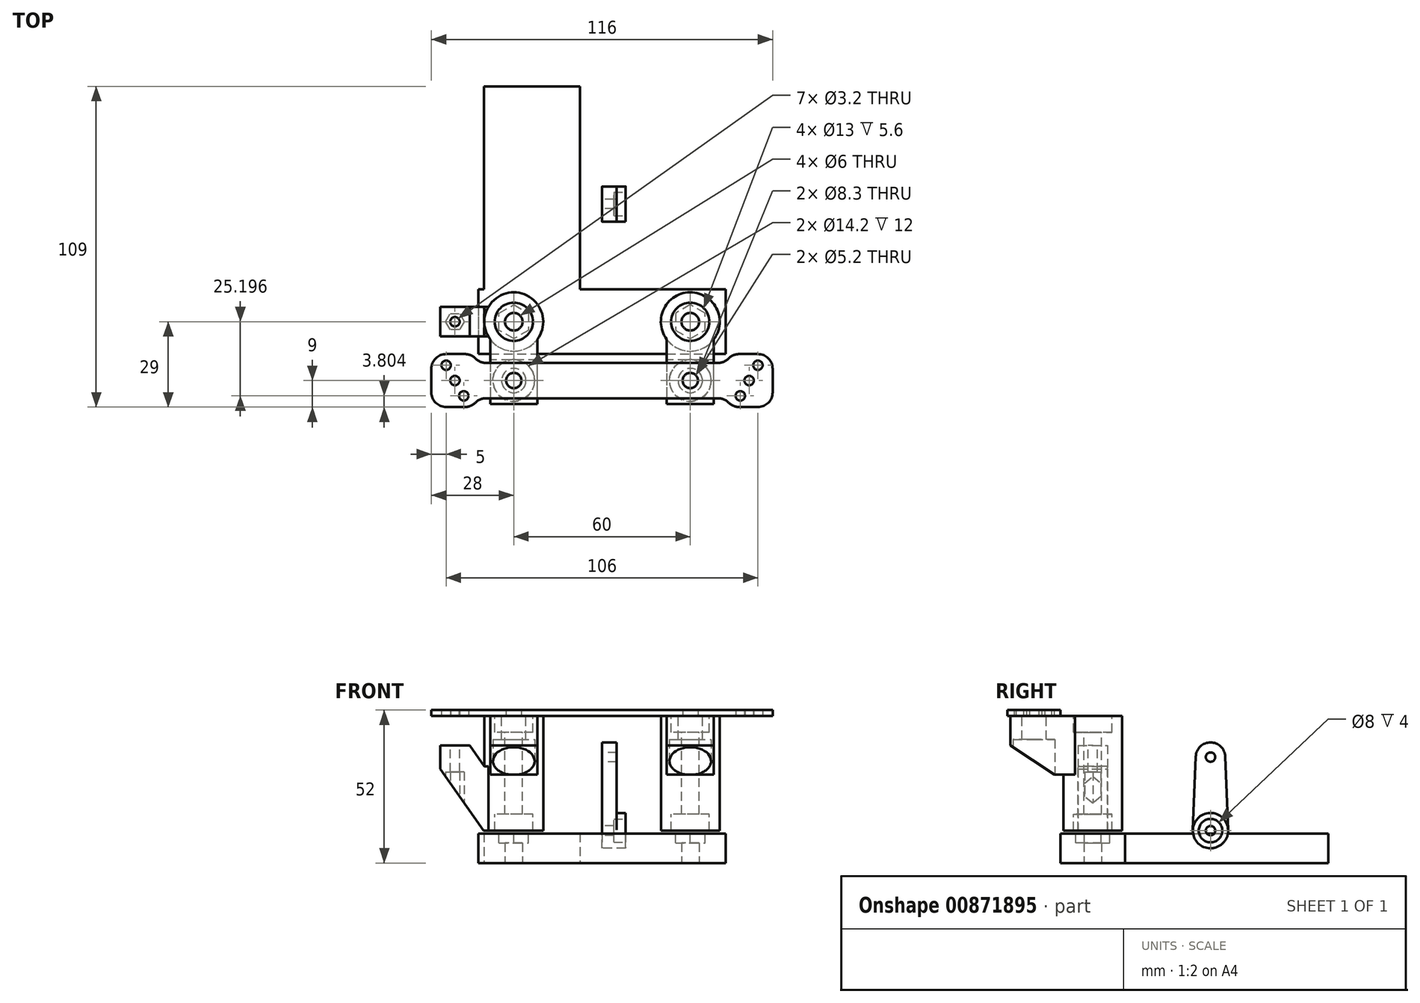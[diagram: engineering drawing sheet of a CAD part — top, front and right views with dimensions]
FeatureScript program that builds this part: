
annotation { "Feature Type Name" : "Feature", "Feature Type Description" : "" }
export const myFeature = defineFeature(function(context is Context, id is Id, definition is map)
    precondition{}
    {
        {
            var Q0;
            Q0=qCreatedBy(makeId("Top.planeOp"),FACE);
            var sketch = newSketch(context, id + "F0", { "sketchPlane" : qUnion([Q0])});
            skCircle(sketch, "E0", {"center": v(-30, 0) * mm, "radius": 3 * mm});
            skCircle(sketch, "E1", {"center": v(30, 0) * mm, "radius": 3 * mm});
            skLineSegment(sketch, "E2.bottom", {"start": v(-42, 11) * mm, "end": v(42, 11) * mm});
            skLineSegment(sketch, "E2.top", {"start": v(-42, -11) * mm, "end": v(42, -11) * mm});
            skLineSegment(sketch, "E2.left", {"start": v(-42, 11) * mm, "end": v(-42, -11) * mm});
            skLineSegment(sketch, "E2.right", {"start": v(42, 11) * mm, "end": v(42, -11) * mm});
            skPoint(sketch, "E2.middle", {"position": v(0, 0) * mm});
            skLineSegment(sketch, "E3", {"start": v(-30, 0) * mm, "end": v(30, 0) * mm, "construction": true});
            skSolve(sketch);
        }
        {
            var Q0;
            Q0=qSketchRegion(id+"F0",true);
            extrude(context, id + "F1", {"entities" : qUnion([Q0]), "depth" : 10 * mm, "offsetDistance" : 25 * mm});
        }
        {
            var Q0;
            Q0=makeQuery(id+"F1.opExtrude","CAP_FACE",FACE,{"disambiguationData":[OSD([sQuery(id+"F0.wireOp",EDGE,"E0"),sQuery(id+"F0.wireOp",EDGE,"E1"),sQuery(id+"F0.wireOp",EDGE,"E2.bottom"),sQuery(id+"F0.wireOp",EDGE,"E2.top"),sQuery(id+"F0.wireOp",EDGE,"E2.left"),sQuery(id+"F0.wireOp",EDGE,"E2.right")])],"isStart":false});
            var sketch = newSketch(context, id + "F2", { "sketchPlane" : qUnion([Q0])});
            skCircle(sketch, "E4.cCircle", {"center": v(-30, 0) * mm, "radius": 5 * mm, "construction": true});
            skLineSegment(sketch, "E4.0", {"start": v(-25, 2.89) * mm, "end": v(-25, -2.89) * mm});
            skLineSegment(sketch, "E4.1", {"start": v(-25, -2.89) * mm, "end": v(-30, -5.77) * mm});
            skLineSegment(sketch, "E4.2", {"start": v(-30, -5.77) * mm, "end": v(-35, -2.89) * mm});
            skLineSegment(sketch, "E4.3", {"start": v(-35, -2.89) * mm, "end": v(-35, 2.89) * mm});
            skLineSegment(sketch, "E4.4", {"start": v(-35, 2.89) * mm, "end": v(-30, 5.77) * mm});
            skLineSegment(sketch, "E4.5", {"start": v(-30, 5.77) * mm, "end": v(-25, 2.89) * mm});
            skPoint(sketch, "E4.0.midPoint", {"position": v(-25, 0) * mm});
            skLineSegment(sketch, "E5", {"start": v(0, 0) * mm, "end": v(0, 13.19) * mm, "construction": true});
            skLineSegment(sketch, "E6.MirrorCS", {"start": v(25, -2.89) * mm, "end": v(30, -5.77) * mm});
            skLineSegment(sketch, "E7.MirrorCS", {"start": v(35, 2.89) * mm, "end": v(30, 5.77) * mm});
            skPoint(sketch, "E8.MirrorP", {"position": v(25, 0) * mm});
            skCircle(sketch, "E9.MirrorC", {"center": v(30, 0) * mm, "radius": 5 * mm, "construction": true});
            skLineSegment(sketch, "E10.MirrorCS", {"start": v(25, 2.89) * mm, "end": v(25, -2.89) * mm});
            skLineSegment(sketch, "E11.MirrorCS", {"start": v(30, -5.77) * mm, "end": v(35, -2.89) * mm});
            skLineSegment(sketch, "E12.MirrorCS", {"start": v(35, -2.89) * mm, "end": v(35, 2.89) * mm});
            skLineSegment(sketch, "E13.MirrorCS", {"start": v(30, 5.77) * mm, "end": v(25, 2.89) * mm});
            skSolve(sketch);
        }
        {
            var Q0;
            Q0=qSketchRegion(id+"F2",true);
            extrude(context, id + "F3", {"entities" : qUnion([Q0]), "operationType" : NewBodyOperationType.REMOVE, "oppositeDirection" : true, "depth" : 3.2 * mm, "offsetDistance" : 25 * mm});
        }
        {
            var Q0;
            Q0=qCreatedBy(makeId("Front.planeOp"),FACE);
            var sketch = newSketch(context, id + "F4", { "sketchPlane" : qUnion([Q0])});
            skLineSegment(sketch, "E14", {"start": v(-30, 31.7) * mm, "end": v(-30, -19.85) * mm, "construction": true});
            skLineSegment(sketch, "E15", {"start": v(0, 0) * mm, "end": v(0, 44.27) * mm, "construction": true});
            skLineSegment(sketch, "E16.bottom", {"start": v(-40, 11) * mm, "end": v(-36.5, 11) * mm});
            skLineSegment(sketch, "E16.top", {"start": v(-40, 50) * mm, "end": v(-36.5, 50) * mm});
            skLineSegment(sketch, "E16.left", {"start": v(-40, 11) * mm, "end": v(-40, 50) * mm});
            skLineSegment(sketch, "E17.right", {"start": v(-36.5, 11) * mm, "end": v(-36.5, 16.6) * mm});
            skLineSegment(sketch, "E18", {"start": v(-33, 44.4) * mm, "end": v(-33, 16.6) * mm});
            skLineSegment(sketch, "E19.trimOffspring", {"start": v(-33, 16.6) * mm, "end": v(-36.5, 16.6) * mm});
            skLineSegment(sketch, "E20", {"start": v(-40, 30.5) * mm, "end": v(-16.74, 30.5) * mm, "construction": true});
            skLineSegment(sketch, "E21.MirrorCS", {"start": v(-33, 44.4) * mm, "end": v(-36.5, 44.4) * mm});
            skLineSegment(sketch, "E22.MirrorCS", {"start": v(-36.5, 50) * mm, "end": v(-36.5, 44.4) * mm});
            skSolve(sketch);
        }
        {
            var Q0;
            Q0=makeQuery(id+"F4.imprint","IMPRINT",FACE,{"disambiguationData":[TD([[makeQuery(id+"F4.imprint","IMPRINT",EDGE,{"derivedFrom":sQuery(id+"F4.wireOp",EDGE,"E16.bottom")}),1.0]])]});
            var Q1;
            Q1=sQuery(id+"F4.wireOp",EDGE,"E14");
            revolve(context, id + "F5", {"surfaceOperationType" : NewSurfaceOperationType.NEW, "entities" : qUnion([Q0]), "axis" : qUnion([Q1]), "revolveType" : RevolveType.FULL});
        }
        {
            var Q0;
            Q0=makeQuery(id+"F5.opRevolve","SWEPT_FACE",FACE,{"disambiguationData":[OSD([sQuery(id+"F4.wireOp",EDGE,"E16.top")])]});
            var sketch = newSketch(context, id + "F6", { "sketchPlane" : qUnion([Q0])});
            skArc(sketch, "E23.0", {"start": v(-38, -6) * mm, "mid": v(-30, -10) * mm, "end": v(-22, -6) * mm});
            skLineSegment(sketch, "E24", {"start": v(-38, -6) * mm, "end": v(-38, -28) * mm});
            skLineSegment(sketch, "E25", {"start": v(-38, -28) * mm, "end": v(-22, -28) * mm});
            skLineSegment(sketch, "E26", {"start": v(-22, -28) * mm, "end": v(-22, -6) * mm});
            skLineSegment(sketch, "E27", {"start": v(-30, 0) * mm, "end": v(-30, -20) * mm, "construction": true});
            skCircle(sketch, "E28", {"center": v(-30, -20) * mm, "radius": 4.15 * mm});
            skSolve(sketch);
        }
        {
            var Q0;
            Q0=qSketchRegion(id+"F6",true);
            extrude(context, id + "F7", {"entities" : qUnion([Q0]), "operationType" : NewBodyOperationType.ADD, "oppositeDirection" : true, "depth" : 20 * mm, "offsetDistance" : 25 * mm});
        }
        {
            var Q0;
            Q0=makeQuery(id+"F7.opExtrude","CAP_EDGE",EDGE,{"disambiguationData":[OSD([sQuery(id+"F6.wireOp",EDGE,"E25")])],"isStart":false});
            chamfer(context, id + "F8", {"entities" : qUnion([Q0]), "chamferType" : ChamferType.TWO_OFFSETS, "width1" : 10 * mm, "oppositeDirection" : false, "width2" : 15 * mm, "tangentPropagation" : true});
        }
        {
            var Q0;
            Q0=makeQuery(id+"F7.opExtrude","CAP_FACE",FACE,{"disambiguationData":[OSD([sQuery(id+"F6.wireOp",EDGE,"E23.0"),sQuery(id+"F6.wireOp",EDGE,"E24"),sQuery(id+"F6.wireOp",EDGE,"E25"),sQuery(id+"F6.wireOp",EDGE,"E26"),sQuery(id+"F6.wireOp",EDGE,"E28")])],"isStart":false});
            var sketch = newSketch(context, id + "F9", { "sketchPlane" : qUnion([Q0])});
            skCircle(sketch, "E29.0", {"center": v(-30, 20) * mm, "radius": 4.15 * mm, "construction": true});
            skCircle(sketch, "E30.cCircle", {"center": v(-30, 20) * mm, "radius": 7.1 * mm});
            skLineSegment(sketch, "E30.0", {"start": v(-34.1, 27.1) * mm, "end": v(-25.9, 27.1) * mm, "construction": true});
            skLineSegment(sketch, "E30.1", {"start": v(-25.9, 27.1) * mm, "end": v(-21.8, 20) * mm, "construction": true});
            skLineSegment(sketch, "E30.2", {"start": v(-21.8, 20) * mm, "end": v(-25.9, 12.9) * mm, "construction": true});
            skLineSegment(sketch, "E30.3", {"start": v(-25.9, 12.9) * mm, "end": v(-34.1, 12.9) * mm, "construction": true});
            skLineSegment(sketch, "E30.4", {"start": v(-34.1, 12.9) * mm, "end": v(-38.2, 20) * mm, "construction": true});
            skLineSegment(sketch, "E30.5", {"start": v(-38.2, 20) * mm, "end": v(-34.1, 27.1) * mm, "construction": true});
            skPoint(sketch, "E30.0.midPoint", {"position": v(-30, 27.1) * mm});
            skSolve(sketch);
        }
        {
            var Q0;
            Q0=qSketchRegion(id+"F9",true);
            extrude(context, id + "F10", {"entities" : qUnion([Q0]), "operationType" : NewBodyOperationType.REMOVE, "oppositeDirection" : true, "depth" : 12 * mm, "offsetDistance" : 25 * mm});
        }
        {
            var Q0;
            Q0=makeQuery(id+"F5.opRevolve","SWEPT_BODY",BODY,{"disambiguationData":[OSD([sQuery(id+"F4.wireOp",EDGE,"E16.bottom"),sQuery(id+"F4.wireOp",EDGE,"E16.top"),sQuery(id+"F4.wireOp",EDGE,"E16.left"),sQuery(id+"F4.wireOp",EDGE,"E17.right"),sQuery(id+"F4.wireOp",EDGE,"E18"),sQuery(id+"F4.wireOp",EDGE,"E19.trimOffspring"),sQuery(id+"F4.wireOp",EDGE,"E21.MirrorCS"),sQuery(id+"F4.wireOp",EDGE,"E22.MirrorCS")])]});
            transform(context, id + "F11", {"entities" : qUnion([Q0]), "transformType" : TransformType.TRANSLATION_3D, "dx" : 60 * mm, "dy" : 0 * mm, "dz" : 0 * mm, "makeCopy" : true});
        }
        {
            var Q0;
            Q0=makeQuery(id+"F11.opPattern","COPY",FACE,{"derivedFrom":makeQuery(id+"F7.boolean.opBoolean","MERGE",FACE,{"derivedFrom":[makeQuery(id+"F5.opRevolve","SWEPT_FACE",FACE,{"disambiguationData":[OSD([sQuery(id+"F4.wireOp",EDGE,"E16.top")])]}),makeQuery(id+"F7.opExtrude","CAP_FACE",FACE,{"disambiguationData":[OSD([sQuery(id+"F6.wireOp",EDGE,"E23.0"),sQuery(id+"F6.wireOp",EDGE,"E24"),sQuery(id+"F6.wireOp",EDGE,"E25"),sQuery(id+"F6.wireOp",EDGE,"E26"),sQuery(id+"F6.wireOp",EDGE,"E28")])],"isStart":true})]}),"instanceName":"1"});
            var sketch = newSketch(context, id + "F12", { "sketchPlane" : qUnion([Q0])});
            skLineSegment(sketch, "E31", {"start": v(-50, -20) * mm, "end": v(50, -20) * mm, "construction": true});
            skLineSegment(sketch, "E32", {"start": v(0, 0) * mm, "end": v(0, -26) * mm, "construction": true});
            skLineSegment(sketch, "E33.bottom", {"start": v(42, -26) * mm, "end": v(0, -26) * mm});
            skPoint(sketch, "E33.middle", {"position": v(0, -20) * mm});
            skLineSegment(sketch, "E34", {"start": v(47, -25.2) * mm, "end": v(53, -14.8) * mm, "construction": true});
            skPoint(sketch, "E34.endSnap0", {"position": v(38, -17) * mm});
            skLineSegment(sketch, "E35.bottom", {"start": v(58, -11) * mm, "end": v(42, -11) * mm});
            skLineSegment(sketch, "E35.top", {"start": v(58, -29) * mm, "end": v(42, -29) * mm});
            skLineSegment(sketch, "E35.right", {"start": v(42, -11) * mm, "end": v(42, -14) * mm});
            skPoint(sketch, "E35.middle", {"position": v(50, -20) * mm});
            skCircle(sketch, "E36", {"center": v(53, -14.8) * mm, "radius": 1.6 * mm});
            skCircle(sketch, "E37", {"center": v(50, -20) * mm, "radius": 1.6 * mm});
            skCircle(sketch, "E38", {"center": v(47, -25.2) * mm, "radius": 1.6 * mm});
            skLineSegment(sketch, "E39.trimOffspring", {"start": v(42, -14) * mm, "end": v(0, -14) * mm});
            skLineSegment(sketch, "E40.trimOffspring", {"start": v(42, -26) * mm, "end": v(42, -29) * mm});
            skLineSegment(sketch, "E41", {"start": v(58, -11) * mm, "end": v(58, -29) * mm});
            skCircle(sketch, "E42.MirrorC", {"center": v(-50, -20) * mm, "radius": 1.6 * mm});
            skLineSegment(sketch, "E43.MirrorCS", {"start": v(-58, -11) * mm, "end": v(-58, -29) * mm});
            skLineSegment(sketch, "E44.MirrorCS", {"start": v(-58, -11) * mm, "end": v(-42, -11) * mm});
            skLineSegment(sketch, "E45.MirrorCS", {"start": v(-58, -29) * mm, "end": v(-42, -29) * mm});
            skLineSegment(sketch, "E46.MirrorCS", {"start": v(-42, -14) * mm, "end": v(0, -14) * mm});
            skPoint(sketch, "E47.MirrorP", {"position": v(-38, -17) * mm});
            skCircle(sketch, "E48.MirrorC", {"center": v(-53, -14.8) * mm, "radius": 1.6 * mm});
            skLineSegment(sketch, "E49.MirrorCS", {"start": v(-42, -26) * mm, "end": v(-42, -29) * mm});
            skLineSegment(sketch, "E50.MirrorCS", {"start": v(-47, -25.2) * mm, "end": v(-53, -14.8) * mm, "construction": true});
            skLineSegment(sketch, "E51.MirrorCS", {"start": v(-42, -11) * mm, "end": v(-42, -14) * mm});
            skLineSegment(sketch, "E52.MirrorCS", {"start": v(50, -20) * mm, "end": v(-50, -20) * mm, "construction": true});
            skLineSegment(sketch, "E53.MirrorCS", {"start": v(-42, -26) * mm, "end": v(0, -26) * mm});
            skCircle(sketch, "E54.MirrorC", {"center": v(-47, -25.2) * mm, "radius": 1.6 * mm});
            skCircle(sketch, "E55.0", {"center": v(30, -20) * mm, "radius": 4.15 * mm, "construction": true});
            skCircle(sketch, "E56.0", {"center": v(-30, -20) * mm, "radius": 4.15 * mm, "construction": true});
            skCircle(sketch, "E57", {"center": v(-30, -20) * mm, "radius": 2.6 * mm});
            skCircle(sketch, "E58", {"center": v(30, -20) * mm, "radius": 2.6 * mm});
            skSolve(sketch);
        }
        {
            var Q0;
            Q0=qSketchRegion(id+"F12",true);
            extrude(context, id + "F13", {"entities" : qUnion([Q0]), "depth" : 2 * mm, "offsetDistance" : 25 * mm});
        }
        {
            var Q0;
            Q0=makeQuery(id+"F13.opExtrude","SWEPT_EDGE",EDGE,{"disambiguationData":[OSD([sQuery(id+"F12.wireOp",EDGE,"E43.MirrorCS"),sQuery(id+"F12.wireOp",EDGE,"E45.MirrorCS")])]});
            var Q1;
            Q1=makeQuery(id+"F13.opExtrude","SWEPT_EDGE",EDGE,{"disambiguationData":[OSD([sQuery(id+"F12.wireOp",EDGE,"E45.MirrorCS"),sQuery(id+"F12.wireOp",EDGE,"E49.MirrorCS")])]});
            var Q2;
            Q2=makeQuery(id+"F13.opExtrude","SWEPT_EDGE",EDGE,{"disambiguationData":[OSD([sQuery(id+"F12.wireOp",EDGE,"E43.MirrorCS"),sQuery(id+"F12.wireOp",EDGE,"E44.MirrorCS")])]});
            var Q3;
            Q3=makeQuery(id+"F13.opExtrude","SWEPT_EDGE",EDGE,{"disambiguationData":[OSD([sQuery(id+"F12.wireOp",EDGE,"E44.MirrorCS"),sQuery(id+"F12.wireOp",EDGE,"E51.MirrorCS")])]});
            var Q4;
            Q4=makeQuery(id+"F13.opExtrude","SWEPT_EDGE",EDGE,{"disambiguationData":[OSD([sQuery(id+"F12.wireOp",EDGE,"E35.top"),sQuery(id+"F12.wireOp",EDGE,"E40.trimOffspring")])]});
            var Q5;
            Q5=makeQuery(id+"F13.opExtrude","SWEPT_EDGE",EDGE,{"disambiguationData":[OSD([sQuery(id+"F12.wireOp",EDGE,"E35.top"),sQuery(id+"F12.wireOp",EDGE,"E41")])]});
            var Q6;
            Q6=makeQuery(id+"F13.opExtrude","SWEPT_EDGE",EDGE,{"disambiguationData":[OSD([sQuery(id+"F12.wireOp",EDGE,"E35.bottom"),sQuery(id+"F12.wireOp",EDGE,"E35.right")])]});
            var Q7;
            Q7=makeQuery(id+"F13.opExtrude","SWEPT_EDGE",EDGE,{"disambiguationData":[OSD([sQuery(id+"F12.wireOp",EDGE,"E35.bottom"),sQuery(id+"F12.wireOp",EDGE,"E41")])]});
            fillet(context, id + "F14", {"entities" : qUnion([Q0, Q1, Q2, Q3, Q4, Q5, Q6, Q7]), "radius" : 5 * mm, "tangentPropagation" : true, "allowEdgeOverflow" : false});
        }
        {
            var Q0;
            Q0=makeQuery(id+"F14.opFillet","BLEND_EDGE",EDGE,{"blendedFrom":[makeQuery(id+"F13.opExtrude","SWEPT_EDGE",EDGE,{"disambiguationData":[OSD([sQuery(id+"F12.wireOp",EDGE,"E35.top"),sQuery(id+"F12.wireOp",EDGE,"E40.trimOffspring")])]}),makeQuery(id+"F13.opExtrude","SWEPT_FACE",FACE,{"disambiguationData":[OSD([sQuery(id+"F12.wireOp",EDGE,"E33.bottom"),sQuery(id+"F12.wireOp",EDGE,"E53.MirrorCS")])]})],"blendedInto":[makeQuery(id+"F13.opExtrude","SWEPT_FACE",FACE,{"disambiguationData":[OSD([sQuery(id+"F12.wireOp",EDGE,"E33.bottom"),sQuery(id+"F12.wireOp",EDGE,"E53.MirrorCS")])]})]});
            var Q1;
            Q1=makeQuery(id+"F14.opFillet","BLEND_EDGE",EDGE,{"blendedFrom":[makeQuery(id+"F13.opExtrude","SWEPT_EDGE",EDGE,{"disambiguationData":[OSD([sQuery(id+"F12.wireOp",EDGE,"E35.bottom"),sQuery(id+"F12.wireOp",EDGE,"E35.right")])]}),makeQuery(id+"F13.opExtrude","SWEPT_FACE",FACE,{"disambiguationData":[OSD([sQuery(id+"F12.wireOp",EDGE,"E39.trimOffspring"),sQuery(id+"F12.wireOp",EDGE,"E46.MirrorCS")])]})],"blendedInto":[makeQuery(id+"F13.opExtrude","SWEPT_FACE",FACE,{"disambiguationData":[OSD([sQuery(id+"F12.wireOp",EDGE,"E39.trimOffspring"),sQuery(id+"F12.wireOp",EDGE,"E46.MirrorCS")])]})]});
            var Q2;
            Q2=makeQuery(id+"F14.opFillet","BLEND_EDGE",EDGE,{"blendedFrom":[makeQuery(id+"F13.opExtrude","SWEPT_EDGE",EDGE,{"disambiguationData":[OSD([sQuery(id+"F12.wireOp",EDGE,"E44.MirrorCS"),sQuery(id+"F12.wireOp",EDGE,"E51.MirrorCS")])]}),makeQuery(id+"F13.opExtrude","SWEPT_FACE",FACE,{"disambiguationData":[OSD([sQuery(id+"F12.wireOp",EDGE,"E39.trimOffspring"),sQuery(id+"F12.wireOp",EDGE,"E46.MirrorCS")])]})],"blendedInto":[makeQuery(id+"F13.opExtrude","SWEPT_FACE",FACE,{"disambiguationData":[OSD([sQuery(id+"F12.wireOp",EDGE,"E39.trimOffspring"),sQuery(id+"F12.wireOp",EDGE,"E46.MirrorCS")])]})]});
            var Q3;
            Q3=makeQuery(id+"F14.opFillet","BLEND_EDGE",EDGE,{"blendedFrom":[makeQuery(id+"F13.opExtrude","SWEPT_EDGE",EDGE,{"disambiguationData":[OSD([sQuery(id+"F12.wireOp",EDGE,"E45.MirrorCS"),sQuery(id+"F12.wireOp",EDGE,"E49.MirrorCS")])]}),makeQuery(id+"F13.opExtrude","SWEPT_FACE",FACE,{"disambiguationData":[OSD([sQuery(id+"F12.wireOp",EDGE,"E33.bottom"),sQuery(id+"F12.wireOp",EDGE,"E53.MirrorCS")])]})],"blendedInto":[makeQuery(id+"F13.opExtrude","SWEPT_FACE",FACE,{"disambiguationData":[OSD([sQuery(id+"F12.wireOp",EDGE,"E33.bottom"),sQuery(id+"F12.wireOp",EDGE,"E53.MirrorCS")])]})]});
            fillet(context, id + "F15", {"entities" : qUnion([Q0, Q1, Q2, Q3]), "radius" : 5 * mm, "tangentPropagation" : true, "allowEdgeOverflow" : false});
        }
        {
            var Q0;
            Q0=qCreatedBy(makeId("Front.planeOp"),FACE);
            var sketch = newSketch(context, id + "F16", { "sketchPlane" : qUnion([Q0])});
            skLineSegment(sketch, "E59", {"start": v(-24, 40) * mm, "end": v(-76, 40) * mm, "construction": true});
            skLineSegment(sketch, "E60", {"start": v(-50, 40) * mm, "end": v(-50, 32) * mm, "construction": true});
            skLineSegment(sketch, "E61", {"start": v(-40, 11) * mm, "end": v(-40, 50) * mm, "construction": true});
            skLineSegment(sketch, "E62.bottom", {"start": v(-45, 40) * mm, "end": v(-55, 40) * mm});
            skLineSegment(sketch, "E62.top", {"start": v(-45, 32) * mm, "end": v(-55, 32) * mm, "construction": true});
            skLineSegment(sketch, "E62.left", {"start": v(-45, 40) * mm, "end": v(-45, 32) * mm, "construction": true});
            skLineSegment(sketch, "E62.right", {"start": v(-55, 40) * mm, "end": v(-55, 32) * mm});
            skPoint(sketch, "E62.middle", {"position": v(-50, 36) * mm});
            skLineSegment(sketch, "E63", {"start": v(-45, 40) * mm, "end": v(-40, 32.86) * mm});
            skLineSegment(sketch, "E64", {"start": v(-55, 32) * mm, "end": v(-40, 10.58) * mm});
            skPoint(sketch, "E65", {"position": v(-40, 30.5) * mm});
            skLineSegment(sketch, "E66", {"start": v(-40, 32.86) * mm, "end": v(-37, 32.86) * mm});
            skLineSegment(sketch, "E67", {"start": v(-37, 32.86) * mm, "end": v(-37, 11) * mm});
            skLineSegment(sketch, "E68", {"start": v(-37, 11) * mm, "end": v(-47.24, 11) * mm});
            skSolve(sketch);
        }
        {
            var Q0;
            Q0=qSketchRegion(id+"F16",true);
            extrude(context, id + "F17", {"entities" : qUnion([Q0]), "operationType" : NewBodyOperationType.ADD, "depth" : 10 * mm, "offsetDistance" : 25 * mm, "symmetric" : true});
        }
        {
            var Q0;
            Q0=qCreatedBy(makeId("Right.planeOp"),FACE);
            var sketch = newSketch(context, id + "F18", { "sketchPlane" : qUnion([Q0])});
            skLineSegment(sketch, "E69", {"start": v(40, 11) * mm, "end": v(40, 36) * mm, "construction": true});
            skArc(sketch, "E70", {"start": v(45, 36.2) * mm, "mid": v(40, 41) * mm, "end": v(35, 36.2) * mm});
            skArc(sketch, "E71", {"start": v(34, 11.24) * mm, "mid": v(40, 5) * mm, "end": v(46, 11.24) * mm});
            skCircle(sketch, "E72", {"center": v(40, 36) * mm, "radius": 1.6 * mm});
            skLineSegment(sketch, "E73", {"start": v(46, 11.24) * mm, "end": v(45, 36.2) * mm});
            skLineSegment(sketch, "E74", {"start": v(35, 36.2) * mm, "end": v(34, 11.24) * mm});
            skCircle(sketch, "E75", {"center": v(40, 11) * mm, "radius": 1.6 * mm});
            skSolve(sketch);
        }
        {
            var Q0;
            Q0=makeQuery(id+"F18.imprint","IMPRINT",FACE,{"disambiguationData":[TD([[makeQuery(id+"F18.imprint","IMPRINT",EDGE,{"derivedFrom":sQuery(id+"F18.wireOp",EDGE,"E70")}),1.0]])]});
            extrude(context, id + "F19", {"entities" : qUnion([Q0]), "depth" : 5 * mm, "offsetDistance" : 25 * mm});
        }
        {
            var Q0;
            Q0=makeQuery(id+"F19.opExtrude","CAP_FACE",FACE,{"disambiguationData":[OSD([sQuery(id+"F18.wireOp",EDGE,"E70"),sQuery(id+"F18.wireOp",EDGE,"E71"),sQuery(id+"F18.wireOp",EDGE,"E72"),sQuery(id+"F18.wireOp",EDGE,"E73"),sQuery(id+"F18.wireOp",EDGE,"E74"),sQuery(id+"F18.wireOp",EDGE,"E75")])],"isStart":false});
            var sketch = newSketch(context, id + "F20", { "sketchPlane" : qUnion([Q0])});
            skCircle(sketch, "E76.0", {"center": v(40, 11) * mm, "radius": 1.6 * mm});
            skCircle(sketch, "E77", {"center": v(40, 11) * mm, "radius": 6 * mm});
            skSolve(sketch);
        }
        {
            var Q0;
            Q0=qSketchRegion(id+"F20",true);
            extrude(context, id + "F21", {"entities" : qUnion([Q0]), "operationType" : NewBodyOperationType.ADD, "depth" : 3 * mm, "offsetDistance" : 25 * mm});
        }
        {
            var Q0;
            Q0=makeQuery(id+"F21.opExtrude","CAP_FACE",FACE,{"disambiguationData":[OSD([sQuery(id+"F20.wireOp",EDGE,"E76.0"),sQuery(id+"F20.wireOp",EDGE,"E77")])],"isStart":false});
            var sketch = newSketch(context, id + "F22", { "sketchPlane" : qUnion([Q0])});
            skCircle(sketch, "E78", {"center": v(40, 11) * mm, "radius": 4 * mm});
            skSolve(sketch);
        }
        {
            var Q0;
            Q0=qSketchRegion(id+"F22",true);
            extrude(context, id + "F23", {"entities" : qUnion([Q0]), "operationType" : NewBodyOperationType.REMOVE, "oppositeDirection" : true, "depth" : 4 * mm, "offsetDistance" : 25 * mm});
        }
        {
            var Q0;
            Q0=makeQuery(id+"F17.boolean.opBoolean","MERGE",FACE,{"derivedFrom":[makeQuery(id+"F5.opRevolve","SWEPT_FACE",FACE,{"disambiguationData":[OSD([sQuery(id+"F4.wireOp",EDGE,"E16.bottom")])]}),makeQuery(id+"F17.opExtrude","SWEPT_FACE",FACE,{"disambiguationData":[OSD([sQuery(id+"F16.wireOp",EDGE,"E68")])]})]});
            var sketch = newSketch(context, id + "F24", { "sketchPlane" : qUnion([Q0])});
            skCircle(sketch, "E79.cCircle", {"center": v(-50, 0) * mm, "radius": 2.75 * mm, "construction": true});
            skLineSegment(sketch, "E79.0", {"start": v(-46.82, 0) * mm, "end": v(-48.41, -2.75) * mm});
            skLineSegment(sketch, "E79.1", {"start": v(-48.41, -2.75) * mm, "end": v(-51.59, -2.75) * mm});
            skLineSegment(sketch, "E79.2", {"start": v(-51.59, -2.75) * mm, "end": v(-53.18, 0) * mm});
            skLineSegment(sketch, "E79.3", {"start": v(-53.18, 0) * mm, "end": v(-51.59, 2.75) * mm});
            skLineSegment(sketch, "E79.4", {"start": v(-51.59, 2.75) * mm, "end": v(-48.41, 2.75) * mm});
            skLineSegment(sketch, "E79.5", {"start": v(-48.41, 2.75) * mm, "end": v(-46.82, 0) * mm});
            skPoint(sketch, "E79.0.midPoint", {"position": v(-47.62, -1.38) * mm});
            skLineSegment(sketch, "E80", {"start": v(-30, 0) * mm, "end": v(-50, 0) * mm, "construction": true});
            skSolve(sketch);
        }
        {
            var Q0;
            Q0=qSketchRegion(id+"F24",true);
            extrude(context, id + "F25", {"entities" : qUnion([Q0]), "operationType" : NewBodyOperationType.REMOVE, "oppositeDirection" : true, "depth" : 20 * mm, "offsetDistance" : 25 * mm});
        }
        {
            var Q0;
            Q0=sQuery(id+"F24.wireOp",VERTEX,"E80.end");
            var Q1;
            Q1=makeQuery(id+"F5.opRevolve","SWEPT_BODY",BODY,{"disambiguationData":[OSD([sQuery(id+"F4.wireOp",EDGE,"E16.bottom"),sQuery(id+"F4.wireOp",EDGE,"E16.top"),sQuery(id+"F4.wireOp",EDGE,"E16.left"),sQuery(id+"F4.wireOp",EDGE,"E17.right"),sQuery(id+"F4.wireOp",EDGE,"E18"),sQuery(id+"F4.wireOp",EDGE,"E19.trimOffspring"),sQuery(id+"F4.wireOp",EDGE,"E21.MirrorCS"),sQuery(id+"F4.wireOp",EDGE,"E22.MirrorCS")])]});
            hole(context, id + "F26", {"style" : HoleStyle.SIMPLE, "endStyle" : HoleEndStyle.THROUGH, "holeDiameter" : 3.2 * mm, "majorDiameter" : 5 * mm, "isTappedThrough" : true, "tappedDepth" : 12 * mm, "tapClearance" : 3, "locations" : qUnion([Q0]), "scope" : qUnion([Q1])});
        }
        {
            var Q0;
            Q0=qCreatedBy(makeId("Top.planeOp"),FACE);
            var sketch = newSketch(context, id + "F27", { "sketchPlane" : qUnion([Q0])});
            skLineSegment(sketch, "E81", {"start": v(0, 53) * mm, "end": v(-62, 53) * mm, "construction": true});
            skLineSegment(sketch, "E82.bottom", {"start": v(-11.5, 73.5) * mm, "end": v(-50.5, 73.5) * mm, "construction": true});
            skLineSegment(sketch, "E82.top", {"start": v(-11.5, 32.5) * mm, "end": v(-50.5, 32.5) * mm, "construction": true});
            skLineSegment(sketch, "E82.left", {"start": v(-11.5, 73.5) * mm, "end": v(-11.5, 32.5) * mm, "construction": true});
            skLineSegment(sketch, "E82.right", {"start": v(-50.5, 73.5) * mm, "end": v(-50.5, 32.5) * mm, "construction": true});
            skPoint(sketch, "E82.middle", {"position": v(-31, 53) * mm});
            skLineSegment(sketch, "E83", {"start": v(-40.1, 80) * mm, "end": v(-40.1, 11) * mm});
            skLineSegment(sketch, "E84.0", {"start": v(-42, 11) * mm, "end": v(-42, -11) * mm});
            skLineSegment(sketch, "E85.0", {"start": v(-42, 11) * mm, "end": v(42, 11) * mm});
            skLineSegment(sketch, "E86", {"start": v(-7.5, 11) * mm, "end": v(-7.5, 80) * mm});
            skLineSegment(sketch, "E87", {"start": v(-40.1, 80) * mm, "end": v(-7.5, 80) * mm});
            skSolve(sketch);
        }
        {
            var Q0;
            {var subQ0=sQuery(id+"F27.wireOp",EDGE,"E83");Q0=makeQuery(id+"F27.imprint","IMPRINT",FACE,{"disambiguationData":[TD([[makeQuery(id+"F27.imprint","IMPRINT",EDGE,{"derivedFrom":subQ0}),1.0]])]});}
            var sketch = newSketch(context, id + "F28", { "sketchPlane" : qUnion([Q0])});
            skLineSegment(sketch, "E88.0", {"start": v(-40.1, 80) * mm, "end": v(-7.5, 80) * mm});
            skLineSegment(sketch, "E89.0", {"start": v(-7.5, 11) * mm, "end": v(-7.5, 80) * mm});
            skLineSegment(sketch, "E90.0", {"start": v(-40.1, 80) * mm, "end": v(-40.1, 11) * mm});
            skLineSegment(sketch, "E91.0", {"start": v(-40.1, 11) * mm, "end": v(-7.5, 11) * mm});
            skPoint(sketch, "E92.orphan", {"position": v(-42, 11) * mm});
            skPoint(sketch, "E93.orphan", {"position": v(42, 11) * mm});
            skSolve(sketch);
        }
        {
            var Q0;
            Q0=qSketchRegion(id+"F28",true);
            extrude(context, id + "F29", {"entities" : qUnion([Q0]), "operationType" : NewBodyOperationType.ADD, "depth" : 10 * mm, "offsetDistance" : 25 * mm});
        }
    });
